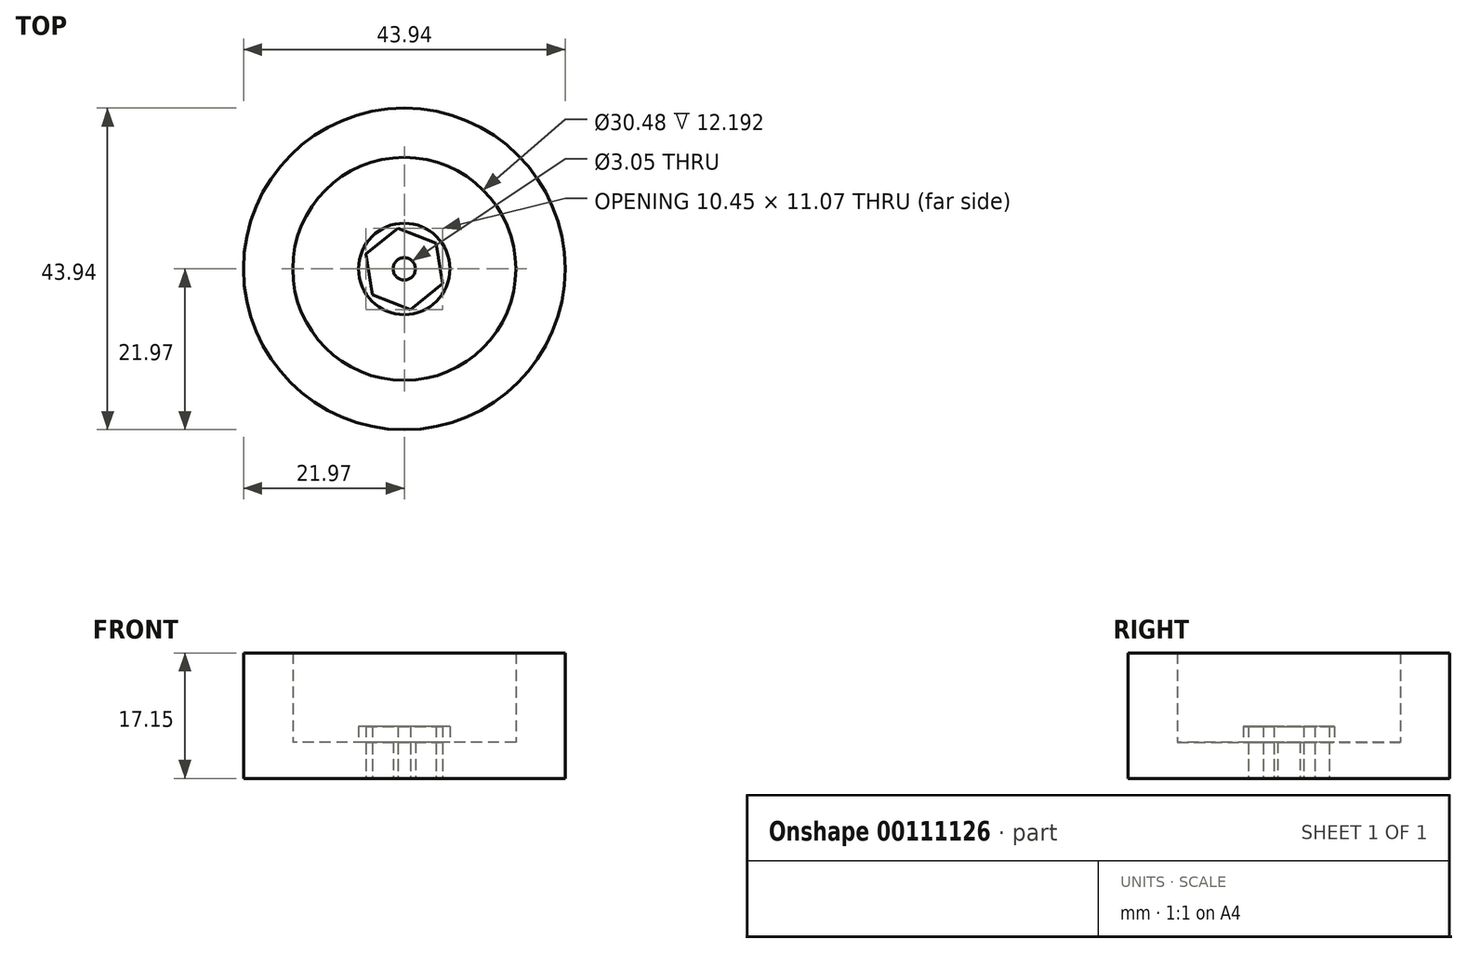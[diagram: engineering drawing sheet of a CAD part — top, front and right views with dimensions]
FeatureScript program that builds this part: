
annotation { "Feature Type Name" : "Feature", "Feature Type Description" : "" }
export const myFeature = defineFeature(function(context is Context, id is Id, definition is map)
    precondition{}
    {
        {
            var Q0;
            Q0=qCreatedBy(makeId("Top.planeOp"),FACE);
            var sketch = newSketch(context, id + "F0", { "sketchPlane" : qUnion([Q0])});
            skCircle(sketch, "E0.cCircle", {"center": v(0, 0) * mm, "radius": 4.85 * mm, "construction": true});
            skLineSegment(sketch, "E0.0", {"start": v(-5.22, 2.02) * mm, "end": v(-0.86, 5.54) * mm});
            skLineSegment(sketch, "E0.1", {"start": v(-0.86, 5.54) * mm, "end": v(4.36, 3.51) * mm});
            skLineSegment(sketch, "E0.2", {"start": v(4.36, 3.51) * mm, "end": v(5.22, -2.02) * mm});
            skLineSegment(sketch, "E0.3", {"start": v(5.22, -2.02) * mm, "end": v(0.86, -5.54) * mm});
            skLineSegment(sketch, "E0.4", {"start": v(0.86, -5.54) * mm, "end": v(-4.36, -3.51) * mm});
            skLineSegment(sketch, "E0.5", {"start": v(-4.36, -3.51) * mm, "end": v(-5.22, 2.02) * mm});
            skPoint(sketch, "E0.0.midPoint", {"position": v(-3.04, 3.78) * mm});
            skCircle(sketch, "E1", {"center": v(0, 0) * mm, "radius": 1.52 * mm});
            skCircle(sketch, "E2", {"center": v(0, 0) * mm, "radius": 6.24 * mm});
            skSolve(sketch);
        }
        {
            var Q0;
            Q0=makeQuery(id+"F0.imprint","IMPRINT",FACE,{"disambiguationData":[TD([[makeQuery(id+"F0.imprint","IMPRINT",EDGE,{"derivedFrom":sQuery(id+"F0.wireOp",EDGE,"E0.0")}),-1.0]])]});
            extrude(context, id + "F1", {"entities" : qUnion([Q0]), "depth" : 4.95 * mm});
        }
        {
            var Q0;
            Q0=qSketchRegion(id+"F0",true);
            extrude(context, id + "F2", {"entities" : qUnion([Q0]), "depth" : 7.11 * mm});
        }
        {
            var Q0;
            Q0=qCreatedBy(makeId("Top.planeOp"),FACE);
            var sketch = newSketch(context, id + "F3", { "sketchPlane" : qUnion([Q0])});
            skCircle(sketch, "E3", {"center": v(0, 0) * mm, "radius": 5.86 * mm});
            skCircle(sketch, "E4", {"center": v(0, 0) * mm, "radius": 15.5 * mm});
            skSolve(sketch);
        }
        {
            var Q0;
            Q0=qSketchRegion(id+"F3",true);
            extrude(context, id + "F4", {"entities" : qUnion([Q0]), "operationType" : NewBodyOperationType.ADD, "depth" : 4.95 * mm});
        }
        {
            var Q0;
            Q0=qCreatedBy(makeId("Top.planeOp"),FACE);
            var sketch = newSketch(context, id + "F5", { "sketchPlane" : qUnion([Q0])});
            skCircle(sketch, "E5", {"center": v(0, 0) * mm, "radius": 15.24 * mm});
            skCircle(sketch, "E6", {"center": v(0, 0) * mm, "radius": 21.97 * mm});
            skSolve(sketch);
        }
        {
            var Q0;
            Q0=qSketchRegion(id+"F5",true);
            extrude(context, id + "F6", {"entities" : qUnion([Q0]), "operationType" : NewBodyOperationType.ADD, "depth" : 17.14 * mm});
        }
    });
